# Revit family: Shower-Shower_Walls-KOHLER-Choreograph-K-97631
name_source: partatom
category: Specialty Equipment
revit_build: Autodesk Revit 2015 (Build: 20140606_1530(x64)
units: mm (PartAtom-declared; Revit-internal decimal feet)

## types (6) — shared parameters
ADA Compliant = No
Assembly Code = C1030200
Date Modified = 12/26/2018
Default Elevation = 0"
Description = 14inch Shower Locker storage
Height = 95 3/16"
Length = 4 1/16"
Manufacturer = KOHLER Co.
MasterFormat 1995 = 10820
MasterFormat 2004 = 10.28.13
Material = Acrylic
Product Documentation Link = http://www.us.kohler.com
Product Name = Choreograph
Product Page URL = http://www.us.kohler.com
URL = https://www.us.kohler.com
Width = 16 13/16"

## per-type parameters (varying)
| type | Finish | Model | Type |
| 0 - White | Kohler-Acrylic-0-White | K-97631-0 | 1 |
| 96 - Biscuit | Kohler-Acrylic-96-Biscuit | K-97631-96 | 2 |
| 47 - Almond | Kohler-Acrylic-47-Almond | K-97631-47 | 3 |
| NY - Dune | Kohler-Acrylic-NY-Dune | K-97631-NY | 4 |
| 95 - Ice Grey | Kohler-Acrylic-95-Ice_Grey | K-97631-95 | 5 |
| G9 - Sandbar | Kohler-Acrylic-G9-Sandbar | K-97631-G9 | 6 |

## geometry (parser evidence)
native form markers: Sweep x6
no freeform markers — native parametric forms only
